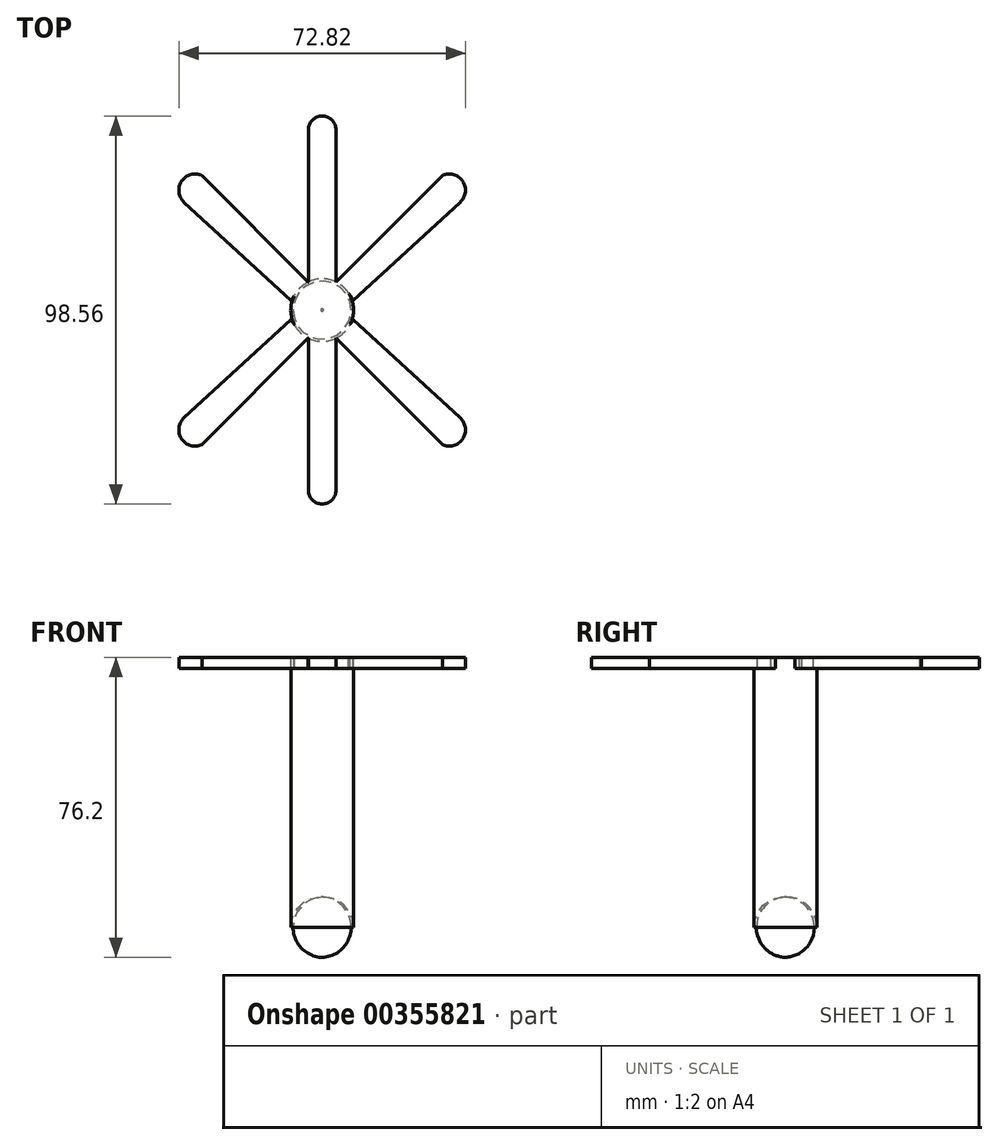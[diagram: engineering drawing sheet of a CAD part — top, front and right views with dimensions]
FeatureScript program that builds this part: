
annotation { "Feature Type Name" : "Feature", "Feature Type Description" : "" }
export const myFeature = defineFeature(function(context is Context, id is Id, definition is map)
    precondition{}
    {
        {
            var Q0;
            Q0=qCreatedBy(makeId("Top.planeOp"),FACE);
            var sketch = newSketch(context, id + "F0", { "sketchPlane" : qUnion([Q0])});
            skCircle(sketch, "E0", {"center": v(0, 0) * mm, "radius": 7.96 * mm});
            skSolve(sketch);
        }
        {
            var Q0;
            Q0=makeQuery(id+"F0.imprint","IMPRINT",FACE,{"disambiguationData":[TD([[makeQuery(id+"F0.imprint","IMPRINT",EDGE,{"derivedFrom":sQuery(id+"F0.wireOp",EDGE,"E0")}),1.0]])]});
            extrude(context, id + "F1", {"entities" : qUnion([Q0]), "oppositeDirection" : true, "depth" : 76.2 * mm});
        }
        {
            var Q0;
            Q0=qCreatedBy(makeId("Top.planeOp"),FACE);
            var sketch = newSketch(context, id + "F2", { "sketchPlane" : qUnion([Q0])});
            skLineSegment(sketch, "E1", {"start": v(-3.5, 7.04) * mm, "end": v(-3.5, 45.77) * mm});
            skLineSegment(sketch, "E2", {"start": v(3.5, 7.12) * mm, "end": v(3.5, 45.77) * mm});
            skArc(sketch, "E3", {"start": v(3.5, 45.77) * mm, "mid": v(0, 49.28) * mm, "end": v(-3.5, 45.77) * mm});
            skArc(sketch, "E4", {"start": v(3.5, 7.12) * mm, "mid": v(0, 7.84) * mm, "end": v(-3.5, 7.04) * mm});
            skLineSegment(sketch, "E5.MirrorCS", {"start": v(-3.5, -7.04) * mm, "end": v(-3.5, -45.77) * mm});
            skLineSegment(sketch, "E6.MirrorCS", {"start": v(3.5, -7.12) * mm, "end": v(3.5, -45.77) * mm});
            skArc(sketch, "E7.MirrorCS", {"start": v(3.5, -45.77) * mm, "mid": v(0, -49.28) * mm, "end": v(-3.5, -45.77) * mm});
            skArc(sketch, "E8.MirrorCS", {"start": v(3.5, -7.12) * mm, "mid": v(0, -7.84) * mm, "end": v(-3.5, -7.04) * mm});
            skLineSegment(sketch, "E9", {"start": v(3.5, 7.12) * mm, "end": v(30.53, 34.22) * mm});
            skLineSegment(sketch, "E10", {"start": v(7.88, 2.47) * mm, "end": v(35.05, 27.36) * mm});
            skArc(sketch, "E11", {"start": v(35.05, 27.36) * mm, "mid": v(35.72, 32.71) * mm, "end": v(30.53, 34.22) * mm});
            skLineSegment(sketch, "E12.MirrorCS", {"start": v(7.88, -2.47) * mm, "end": v(35.05, -27.36) * mm});
            skLineSegment(sketch, "E13.MirrorCS", {"start": v(3.5, -7.12) * mm, "end": v(30.53, -34.22) * mm});
            skArc(sketch, "E14.MirrorCS", {"start": v(35.05, -27.36) * mm, "mid": v(35.72, -32.71) * mm, "end": v(30.53, -34.22) * mm});
            skLineSegment(sketch, "E15.MirrorCS", {"start": v(-3.5, 7.12) * mm, "end": v(-30.53, 34.22) * mm});
            skLineSegment(sketch, "E16.MirrorCS", {"start": v(-7.88, 2.47) * mm, "end": v(-35.05, 27.36) * mm});
            skArc(sketch, "E17.MirrorCS", {"start": v(-35.05, 27.36) * mm, "mid": v(-35.72, 32.71) * mm, "end": v(-30.53, 34.22) * mm});
            skLineSegment(sketch, "E18.MirrorCS", {"start": v(-7.88, -2.47) * mm, "end": v(-35.05, -27.36) * mm});
            skLineSegment(sketch, "E19.MirrorCS", {"start": v(-3.5, -7.12) * mm, "end": v(-30.53, -34.22) * mm});
            skArc(sketch, "E20.MirrorCS", {"start": v(-35.05, -27.36) * mm, "mid": v(-35.72, -32.71) * mm, "end": v(-30.53, -34.22) * mm});
            skArc(sketch, "E21", {"start": v(-3.5, 7.12) * mm, "mid": v(-5.91, 5) * mm, "end": v(-7.88, 2.47) * mm});
            skArc(sketch, "E22", {"start": v(7.88, 2.47) * mm, "mid": v(6, 5.1) * mm, "end": v(3.5, 7.12) * mm});
            skArc(sketch, "E23", {"start": v(3.5, -7.12) * mm, "mid": v(5.92, -5) * mm, "end": v(7.88, -2.47) * mm});
            skArc(sketch, "E24", {"start": v(-7.88, -2.47) * mm, "mid": v(-5.94, -5.03) * mm, "end": v(-3.5, -7.12) * mm});
            skSolve(sketch);
        }
        {
            var Q0;
            Q0=makeQuery(id+"F2.imprint","IMPRINT",FACE,{"disambiguationData":[TD([[makeQuery(id+"F2.imprint","IMPRINT",EDGE,{"derivedFrom":sQuery(id+"F2.wireOp",EDGE,"E1")}),-1.0]])]});
            extrude(context, id + "F3", {"entities" : qUnion([Q0]), "oppositeDirection" : true, "depth" : 1.27 * mm});
        }
        {
            var Q0;
            Q0 = qSketchRegion(id + "F2", true);
            extrude(context, id + "F4", {"entities" : qUnion([Q0]), "operationType" : NewBodyOperationType.ADD, "oppositeDirection" : true, "depth" : 2.8 * mm});
        }
        {
            var Q0;
            Q0=makeQuery(id+"F1.opExtrude","CAP_FACE",FACE,{"disambiguationData":[OSD([sQuery(id+"F0.wireOp",EDGE,"E0")])],"isStart":false});
            fillet(context, id + "F5", {"entities" : qUnion([Q0]), "radius" : 7.67 * mm, "tangentPropagation" : true, "allowEdgeOverflow" : false});
        }
    });
